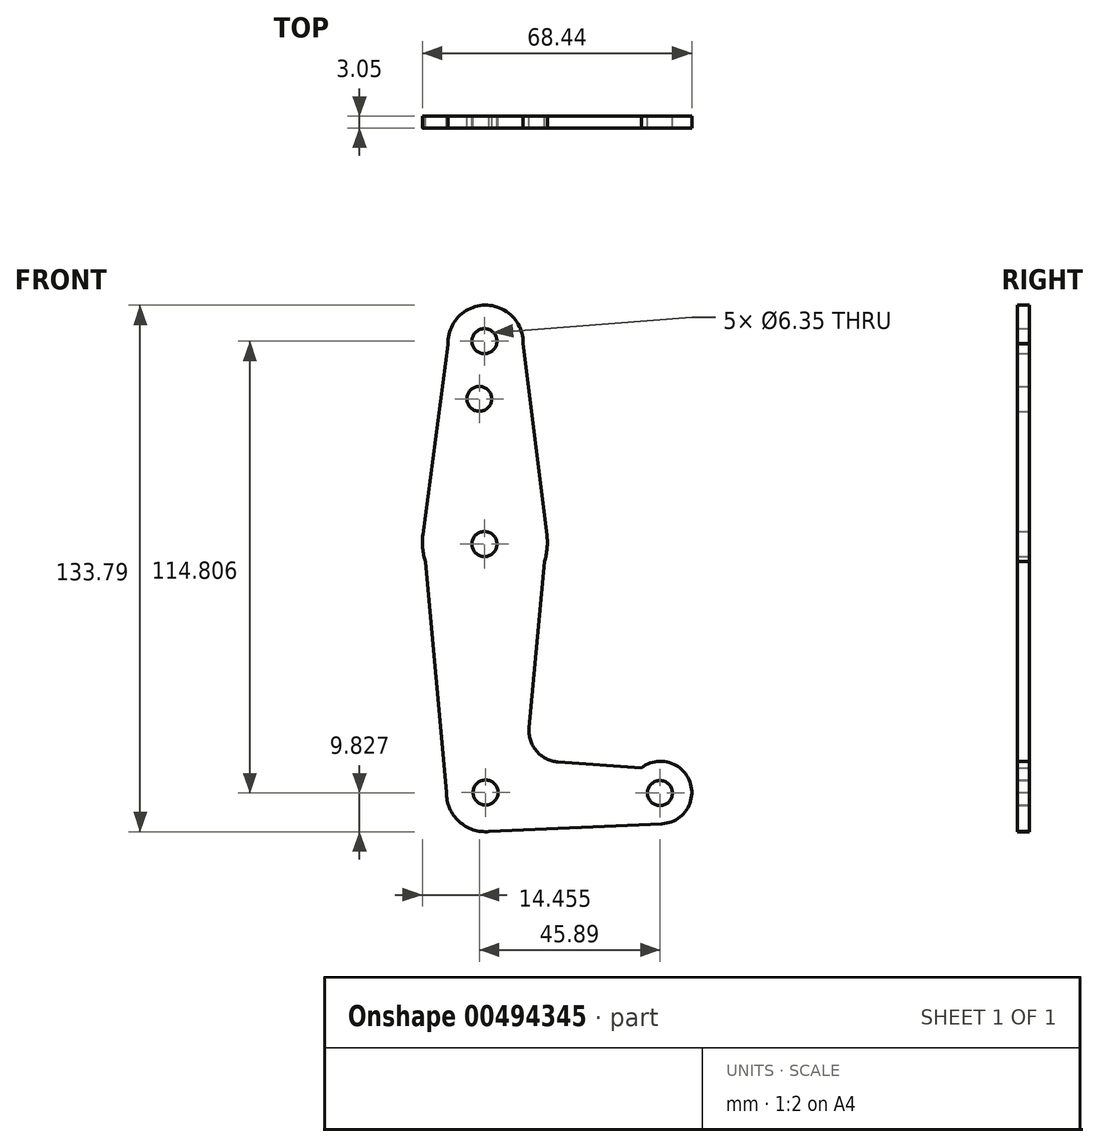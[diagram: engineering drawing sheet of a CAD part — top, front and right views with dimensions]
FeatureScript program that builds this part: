
annotation { "Feature Type Name" : "Feature", "Feature Type Description" : "" }
export const myFeature = defineFeature(function(context is Context, id is Id, definition is map)
    precondition{}
    {
        {
            var Q0;
            Q0=qCreatedBy(makeId("Front.planeOp"),FACE);
            var sketch = newSketch(context, id + "F0", { "sketchPlane" : qUnion([Q0])});
            skLineSegment(sketch, "E0", {"start": v(0, 0) * mm, "end": v(44.45, 0) * mm, "construction": true});
            skCircle(sketch, "E1", {"center": v(44.45, 0) * mm, "radius": 7.94 * mm});
            skCircle(sketch, "E2", {"center": v(-0.18, 63.5) * mm, "radius": 15.88 * mm});
            skCircle(sketch, "E3", {"center": v(0, 114.3) * mm, "radius": 9.53 * mm});
            skLineSegment(sketch, "E4", {"start": v(0, -9.97) * mm, "end": v(44.81, -7.93) * mm});
            skLineSegment(sketch, "E5", {"start": v(-0.18, 63.5) * mm, "end": v(0, 0) * mm, "construction": true});
            skLineSegment(sketch, "E6", {"start": v(0, 114.3) * mm, "end": v(0, 0) * mm, "construction": true});
            skLineSegment(sketch, "E7", {"start": v(18.4, 7.79) * mm, "end": v(39.61, 6.3) * mm});
            skLineSegment(sketch, "E8", {"start": v(9.51, 114.12) * mm, "end": v(15.58, 65.46) * mm});
            skLineSegment(sketch, "E9", {"start": v(15.58, 65.46) * mm, "end": v(11.04, 16.45) * mm});
            skLineSegment(sketch, "E10", {"start": v(-9.52, 113.85) * mm, "end": v(-15.92, 65.58) * mm});
            skLineSegment(sketch, "E11", {"start": v(-9.97, 0) * mm, "end": v(-15.92, 65.58) * mm});
            skPoint(sketch, "E12.newPointB", {"position": v(9.51, 0) * mm});
            skCircle(sketch, "E13", {"center": v(0, 0) * mm, "radius": 3.18 * mm});
            skCircle(sketch, "E14", {"center": v(-0.3, 63.14) * mm, "radius": 3.18 * mm});
            skCircle(sketch, "E15", {"center": v(44.3, -0.14) * mm, "radius": 3.18 * mm});
            skCircle(sketch, "E16", {"center": v(-1.6, 100.02) * mm, "radius": 3.18 * mm});
            skCircle(sketch, "E17", {"center": v(-0.3, 114.66) * mm, "radius": 3.18 * mm});
            skCircle(sketch, "E18", {"center": v(0, 0) * mm, "radius": 9.97 * mm});
            skPoint(sketch, "E19.newPointA", {"position": v(0, 9.08) * mm});
            skArc(sketch, "E19.filletArc", {"start": v(11.04, 16.45) * mm, "mid": v(12.9, 10.57) * mm, "end": v(18.4, 7.79) * mm});
            skSolve(sketch);
        }
        {
            var Q0;
            Q0 = qSketchRegion(id + "F0", true);
            extrude(context, id + "F1", {"entities" : qUnion([Q0]), "depth" : 3.05 * mm});
        }
    });
